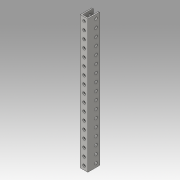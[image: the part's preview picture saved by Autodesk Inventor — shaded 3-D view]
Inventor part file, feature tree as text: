
AUTODESK INVENTOR PART (.ipt)
format: ipt  version: 2016 (Build 200138000, 138)  size: 175,104 bytes
history: native  units: in
note: dims shown in document units (in); Inventor stores cm internally (conversion verified against a paired STEP export)
features: fillet x1
ambient origin geometry x8: Origin, YZ Plane, XZ Plane, XY Plane, X Axis, Y Axis, Z Axis, Center Point
bodies: Solid1 (feature_tree)
feature tree (1):
  fillet  "Fillet1"  [1 undecoded]
note: 1 required parameter value undecoded (feature->parameter linkage not recoverable at this tier; creation-order binding heuristic only, values carry confidence <= 0.55)
